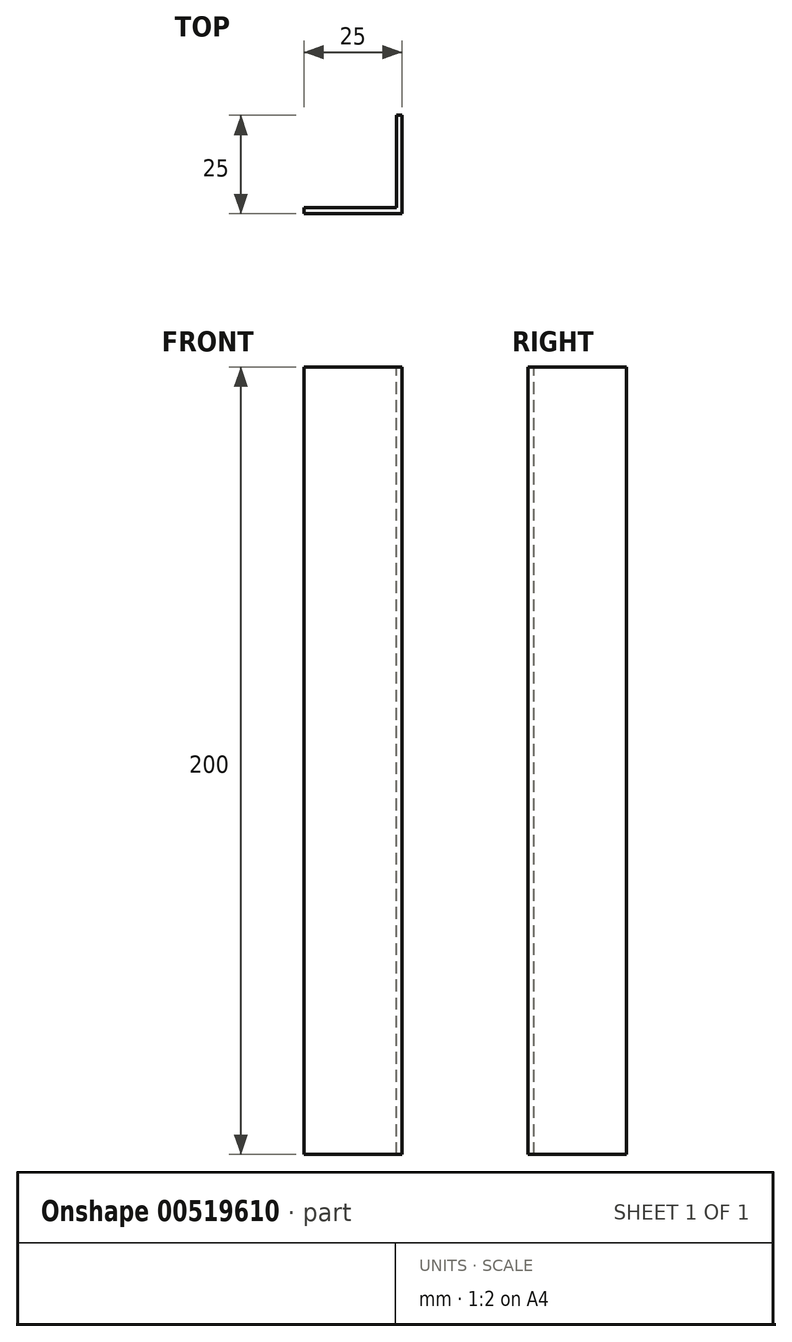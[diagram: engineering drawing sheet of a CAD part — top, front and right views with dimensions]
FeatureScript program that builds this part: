
annotation { "Feature Type Name" : "Feature", "Feature Type Description" : "" }
export const myFeature = defineFeature(function(context is Context, id is Id, definition is map)
    precondition{}
    {
        {
            var Q0;
            Q0=qCreatedBy(makeId("Top.planeOp"),FACE);
            var sketch = newSketch(context, id + "F0", { "sketchPlane" : qUnion([Q0])});
            skLineSegment(sketch, "E0.bottom", {"start": v(12.5, 0.75) * mm, "end": v(-12.5, 0.75) * mm});
            skLineSegment(sketch, "E0.top", {"start": v(12.5, -0.75) * mm, "end": v(-12.5, -0.75) * mm});
            skLineSegment(sketch, "E0.left", {"start": v(12.5, 0.75) * mm, "end": v(12.5, -0.75) * mm});
            skLineSegment(sketch, "E0.right", {"start": v(-12.5, 0.75) * mm, "end": v(-12.5, -0.75) * mm});
            skPoint(sketch, "E0.middle", {"position": v(0, 0) * mm});
            skLineSegment(sketch, "E1.bottom", {"start": v(12.5, -0.75) * mm, "end": v(11, -0.75) * mm});
            skLineSegment(sketch, "E1.top", {"start": v(12.5, 24.25) * mm, "end": v(11, 24.25) * mm});
            skLineSegment(sketch, "E1.left", {"start": v(12.5, -0.75) * mm, "end": v(12.5, 24.25) * mm});
            skLineSegment(sketch, "E1.right", {"start": v(11, -0.75) * mm, "end": v(11, 24.25) * mm});
            skSolve(sketch);
        }
        {
            var Q0;
            Q0=qSketchRegion(id+"F0",true);
            extrude(context, id + "F1", {"entities" : qUnion([Q0]), "oppositeDirection" : true, "depth" : 200 * mm, "offsetDistance" : 25 * mm});
        }
    });
